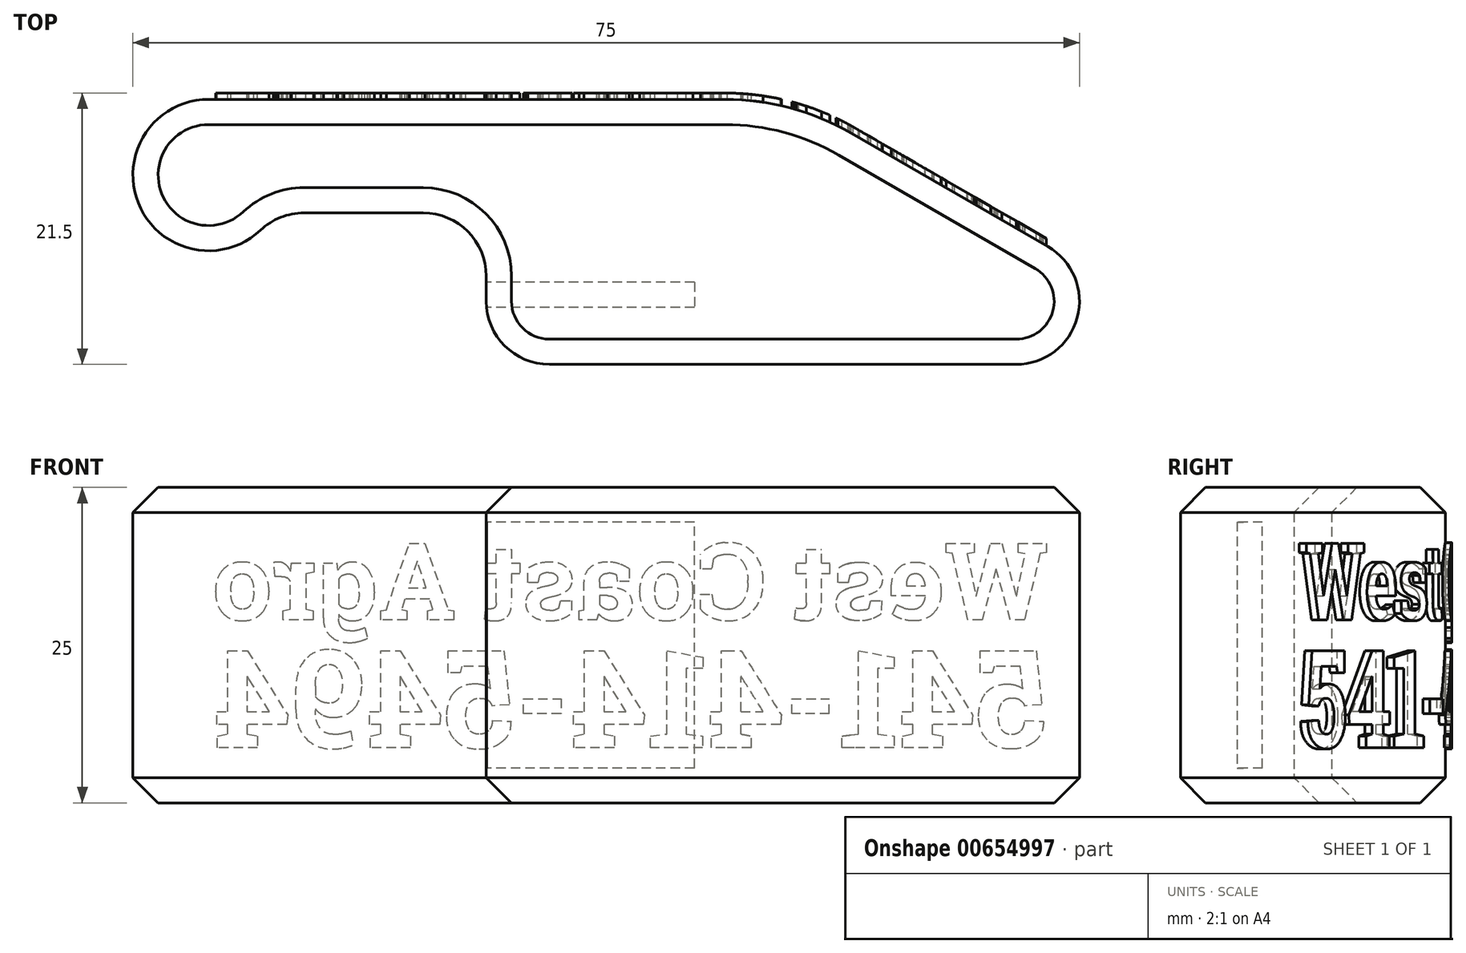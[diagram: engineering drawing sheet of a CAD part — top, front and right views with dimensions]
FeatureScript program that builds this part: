
annotation { "Feature Type Name" : "Feature", "Feature Type Description" : "" }
export const myFeature = defineFeature(function(context is Context, id is Id, definition is map)
    precondition{}
    {
        {
            var Q0;
            Q0=qCreatedBy(makeId("Top.planeOp"),FACE);
            var sketch = newSketch(context, id + "F0", { "sketchPlane" : qUnion([Q0])});
            skLineSegment(sketch, "E0", {"start": v(33.93, 11.32) * mm, "end": v(49.5, 2.33) * mm});
            skLineSegment(sketch, "E1", {"start": v(47, -7) * mm, "end": v(10, -7) * mm});
            skLineSegment(sketch, "E2", {"start": v(5, -2) * mm, "end": v(5, 0) * mm});
            skPoint(sketch, "E3.visualSharp", {"position": v(0, 0) * mm});
            skArc(sketch, "E3.filletArc", {"start": v(5, 0) * mm, "mid": v(3.54, 3.54) * mm, "end": v(0, 5) * mm});
            skPoint(sketch, "E4.visualSharp", {"position": v(33.93, 11.32) * mm});
            skArc(sketch, "E4.filletArc", {"start": v(33.93, 11.32) * mm, "mid": v(29.1, 13.32) * mm, "end": v(23.93, 14) * mm});
            skArc(sketch, "E5.filletArc", {"start": v(47, -7) * mm, "mid": v(51.83, -3.3) * mm, "end": v(49.5, 2.33) * mm});
            skPoint(sketch, "E6.visualSharp", {"position": v(5, -7) * mm});
            skArc(sketch, "E6.filletArc", {"start": v(5, -2) * mm, "mid": v(6.46, -5.54) * mm, "end": v(10, -7) * mm});
            skLineSegment(sketch, "E7", {"start": v(23.93, 14) * mm, "end": v(-17, 14) * mm});
            skLineSegment(sketch, "E8", {"start": v(0, 5) * mm, "end": v(-9.45, 5) * mm});
            skArc(sketch, "E9", {"start": v(-17, 14) * mm, "mid": v(-22.58, 5.78) * mm, "end": v(-12.88, 3.64) * mm});
            skPoint(sketch, "E10.visualSharp", {"position": v(-11.8, 5) * mm});
            skArc(sketch, "E10.filletArc", {"start": v(-9.45, 5) * mm, "mid": v(-11.3, 4.65) * mm, "end": v(-12.88, 3.64) * mm});
            skLineSegment(sketch, "E11", {"start": v(-23, -19.5) * mm, "end": v(-23, 8) * mm, "construction": true});
            skLineSegment(sketch, "E12", {"start": v(52, -19.5) * mm, "end": v(52, -2) * mm, "construction": true});
            skSolve(sketch);
        }
        {
            var Q0;
            Q0=qSketchRegion(id+"F0",true);
            extrude(context, id + "F1", {"entities" : qUnion([Q0]), "endBound" : BoundingType.SYMMETRIC, "depth" : 25 * mm, "offsetDistance" : 25 * mm});
        }
        {
            var Q0;
            Q0=makeQuery(id+"F1.opExtrude","SWEPT_FACE",FACE,{"disambiguationData":[OSD([sQuery(id+"F0.wireOp",EDGE,"E2")])]});
            var sketch = newSketch(context, id + "F2", { "sketchPlane" : qUnion([Q0])});
            skLineSegment(sketch, "E13.bottom", {"start": v(0.5, -9.75) * mm, "end": v(2.5, -9.75) * mm});
            skLineSegment(sketch, "E13.top", {"start": v(0.5, 9.75) * mm, "end": v(2.5, 9.75) * mm});
            skLineSegment(sketch, "E13.left", {"start": v(0.5, -9.75) * mm, "end": v(0.5, 9.75) * mm});
            skLineSegment(sketch, "E13.right", {"start": v(2.5, -9.75) * mm, "end": v(2.5, 9.75) * mm});
            skLineSegment(sketch, "E14", {"start": v(2.5, 12.5) * mm, "end": v(2.5, -12.5) * mm, "construction": true});
            skPoint(sketch, "E15", {"position": v(2.5, 0) * mm});
            skPoint(sketch, "E15.positionSnap0", {"position": v(2.5, 0) * mm});
            skSolve(sketch);
        }
        {
            var Q0;
            Q0=qSketchRegion(id+"F2",true);
            extrude(context, id + "F3", {"entities" : qUnion([Q0]), "operationType" : NewBodyOperationType.REMOVE, "oppositeDirection" : true, "depth" : 16.5 * mm, "offsetDistance" : 25 * mm});
        }
        {
            var Q0;
            Q0=makeQuery(id+"F1.opExtrude","CAP_FACE",FACE,{"disambiguationData":[OSD([sQuery(id+"F0.wireOp",EDGE,"E0"),sQuery(id+"F0.wireOp",EDGE,"E1"),sQuery(id+"F0.wireOp",EDGE,"E2"),sQuery(id+"F0.wireOp",EDGE,"E3.filletArc"),sQuery(id+"F0.wireOp",EDGE,"E4.filletArc"),sQuery(id+"F0.wireOp",EDGE,"E5.filletArc"),sQuery(id+"F0.wireOp",EDGE,"E6.filletArc"),sQuery(id+"F0.wireOp",EDGE,"E7"),sQuery(id+"F0.wireOp",EDGE,"E8"),sQuery(id+"F0.wireOp",EDGE,"E9"),sQuery(id+"F0.wireOp",EDGE,"E10.filletArc")])],"isStart":false});
            var Q1;
            Q1=makeQuery(id+"F1.opExtrude","CAP_FACE",FACE,{"disambiguationData":[OSD([sQuery(id+"F0.wireOp",EDGE,"E0"),sQuery(id+"F0.wireOp",EDGE,"E1"),sQuery(id+"F0.wireOp",EDGE,"E2"),sQuery(id+"F0.wireOp",EDGE,"E3.filletArc"),sQuery(id+"F0.wireOp",EDGE,"E4.filletArc"),sQuery(id+"F0.wireOp",EDGE,"E5.filletArc"),sQuery(id+"F0.wireOp",EDGE,"E6.filletArc"),sQuery(id+"F0.wireOp",EDGE,"E7"),sQuery(id+"F0.wireOp",EDGE,"E8"),sQuery(id+"F0.wireOp",EDGE,"E9"),sQuery(id+"F0.wireOp",EDGE,"E10.filletArc")])],"isStart":true});
            chamfer(context, id + "F4", {"entities" : qUnion([Q0, Q1]), "width" : 2 * mm, "tangentPropagation" : true});
        }
        {
            var Q0;
            Q0=makeQuery(id+"F1.opExtrude","SWEPT_FACE",FACE,{"disambiguationData":[OSD([sQuery(id+"F0.wireOp",EDGE,"E1")])]});
            var sketch = newSketch(context, id + "F5", { "sketchPlane" : qUnion([Q0])});
            skLineSegment(sketch, "E16", {"start": v(44, 10.5) * mm, "end": v(44, -10.5) * mm, "construction": true});
            skCircle(sketch, "E17", {"center": v(44, 0) * mm, "radius": 3 * mm});
            skSolve(sketch);
        }
        {
            var Q0;
            {var subQ0=sQuery(id+"F0.wireOp",EDGE,"E4.filletArc");var subQ2=sQuery(id+"F0.wireOp",EDGE,"E7");Q0=makeQuery(id+"F8.boolean.opBoolean","SPLIT",FACE,{"disambiguationData":[TD([makeQuery(id+"F1.opExtrude","SWEPT_FACE",FACE,{"disambiguationData":[OSD([subQ0])]})])],"derivedFrom":makeQuery(id+"F1.opExtrude","SWEPT_FACE",FACE,{"disambiguationData":[OSD([subQ2])]})});}
            cPlane(context, id + "F6", {"entities" : qUnion([Q0]), "cplaneType" : CPlaneType.OFFSET, "offset" : 3 * mm, "width" : 150 * mm, "height" : 150 * mm});
        }
        {
            var Q0;
            Q0=qCreatedBy(id+"F6.planeOp",FACE);
            var sketch = newSketch(context, id + "F7", { "sketchPlane" : qUnion([Q0])});
            skText(sketch, "E18", { "text": "West Coast Agro", "fontName": "RobotoSlab-Bold.ttf"});
            skText(sketch, "E19", { "text": "541-414-5494", "fontName": "RobotoSlab-Bold.ttf"});
            skLineSegment(sketch, "E20", {"start": v(-16.25, 8.13) * mm, "end": v(-16.25, 10.5) * mm, "construction": true});
            skLineSegment(sketch, "E21", {"start": v(-16.25, -8.13) * mm, "end": v(-16.25, -10.5) * mm, "construction": true});
            skLineSegment(sketch, "E22", {"start": v(-16.25, 2.01) * mm, "end": v(-16.25, -0.36) * mm, "construction": true});
            const initialGuessF7  = {"E18": [-0.0495, 0.00201, 1, 0, 0.00612], "E19": [-0.0495, -0.00813, 1, 0, 0.00778]};
            skSetInitialGuess(sketch, initialGuessF7);
            skSolve(sketch);
        }
        {
            var Q0;
            Q0 = qSketchRegion(id + "F7", true);
            var Q1;
            Q1=makeQuery(id+"F1.opExtrude","SWEPT_FACE",FACE,{"disambiguationData":[OSD([sQuery(id+"F0.wireOp",EDGE,"E0")])]});
            var Q2;
            Q2=makeQuery(id+"F1.opExtrude","SWEPT_FACE",FACE,{"disambiguationData":[OSD([sQuery(id+"F0.wireOp",EDGE,"E7")])]});
            var Q3;
            Q3=makeQuery(id+"F1.opExtrude","SWEPT_BODY",BODY,{"disambiguationData":[OSD([sQuery(id+"F0.wireOp",EDGE,"E0"),sQuery(id+"F0.wireOp",EDGE,"E1"),sQuery(id+"F0.wireOp",EDGE,"E2"),sQuery(id+"F0.wireOp",EDGE,"E3.filletArc"),sQuery(id+"F0.wireOp",EDGE,"E4.filletArc"),sQuery(id+"F0.wireOp",EDGE,"E5.filletArc"),sQuery(id+"F0.wireOp",EDGE,"E6.filletArc"),sQuery(id+"F0.wireOp",EDGE,"E7"),sQuery(id+"F0.wireOp",EDGE,"E8"),sQuery(id+"F0.wireOp",EDGE,"E9"),sQuery(id+"F0.wireOp",EDGE,"E10.filletArc")])]});
            extrude(context, id + "F8", {"entities" : qUnion([Q0, Q1]), "operationType" : NewBodyOperationType.ADD, "endBound" : BoundingType.UP_TO_BODY, "oppositeDirection" : true, "depth" : 2 * mm, "endBoundEntityFace" : qUnion([Q2]), "endBoundEntityBody" : qUnion([Q3]), "offsetDistance" : 25 * mm});
        }
        {
            var Q0;
            Q0=qCreatedBy(makeId("Top.planeOp"),FACE);
            var sketch = newSketch(context, id + "F9", { "sketchPlane" : qUnion([Q0])});
            skArc(sketch, "E23.0", {"start": v(47, -7.5) * mm, "mid": v(52.31, -3.42) * mm, "end": v(49.75, 2.76) * mm});
            skLineSegment(sketch, "E23.1", {"start": v(10, -7.5) * mm, "end": v(47, -7.5) * mm});
            skArc(sketch, "E23.2", {"start": v(4.5, -2) * mm, "mid": v(6.11, -5.89) * mm, "end": v(10, -7.5) * mm});
            skLineSegment(sketch, "E23.3", {"start": v(4.5, 0) * mm, "end": v(4.5, -2) * mm});
            skArc(sketch, "E23.4", {"start": v(0, 4.5) * mm, "mid": v(3.18, 3.18) * mm, "end": v(4.5, 0) * mm});
            skLineSegment(sketch, "E23.5", {"start": v(49.75, 2.76) * mm, "end": v(34.18, 11.75) * mm});
            skArc(sketch, "E23.6", {"start": v(34.18, 11.75) * mm, "mid": v(29.23, 13.8) * mm, "end": v(23.93, 14.5) * mm});
            skLineSegment(sketch, "E23.7", {"start": v(23.93, 14.5) * mm, "end": v(-17, 14.5) * mm});
            skArc(sketch, "E23.8", {"start": v(-17, 14.5) * mm, "mid": v(-23.04, 5.6) * mm, "end": v(-12.54, 3.27) * mm});
            skArc(sketch, "E23.9", {"start": v(-12.54, 3.27) * mm, "mid": v(-11.11, 4.18) * mm, "end": v(-9.45, 4.5) * mm});
            skLineSegment(sketch, "E23.10", {"start": v(-9.45, 4.5) * mm, "end": v(0, 4.5) * mm});
            skLineSegment(sketch, "E24.bottom", {"start": v(-37.23, 24.28) * mm, "end": v(76.8, 24.28) * mm});
            skLineSegment(sketch, "E24.top", {"start": v(-37.23, -31.14) * mm, "end": v(76.8, -31.14) * mm});
            skLineSegment(sketch, "E24.left", {"start": v(-37.23, 24.28) * mm, "end": v(-37.23, -31.14) * mm});
            skLineSegment(sketch, "E24.right", {"start": v(76.8, 24.28) * mm, "end": v(76.8, -31.14) * mm});
            skSolve(sketch);
        }
        {
            var Q0;
            Q0 = qSketchRegion(id + "F9", true);
            extrude(context, id + "F10", {"entities" : qUnion([Q0]), "operationType" : NewBodyOperationType.REMOVE, "endBound" : BoundingType.SYMMETRIC, "oppositeDirection" : true, "depth" : 50 * mm, "offsetDistance" : 25 * mm});
        }
    });
